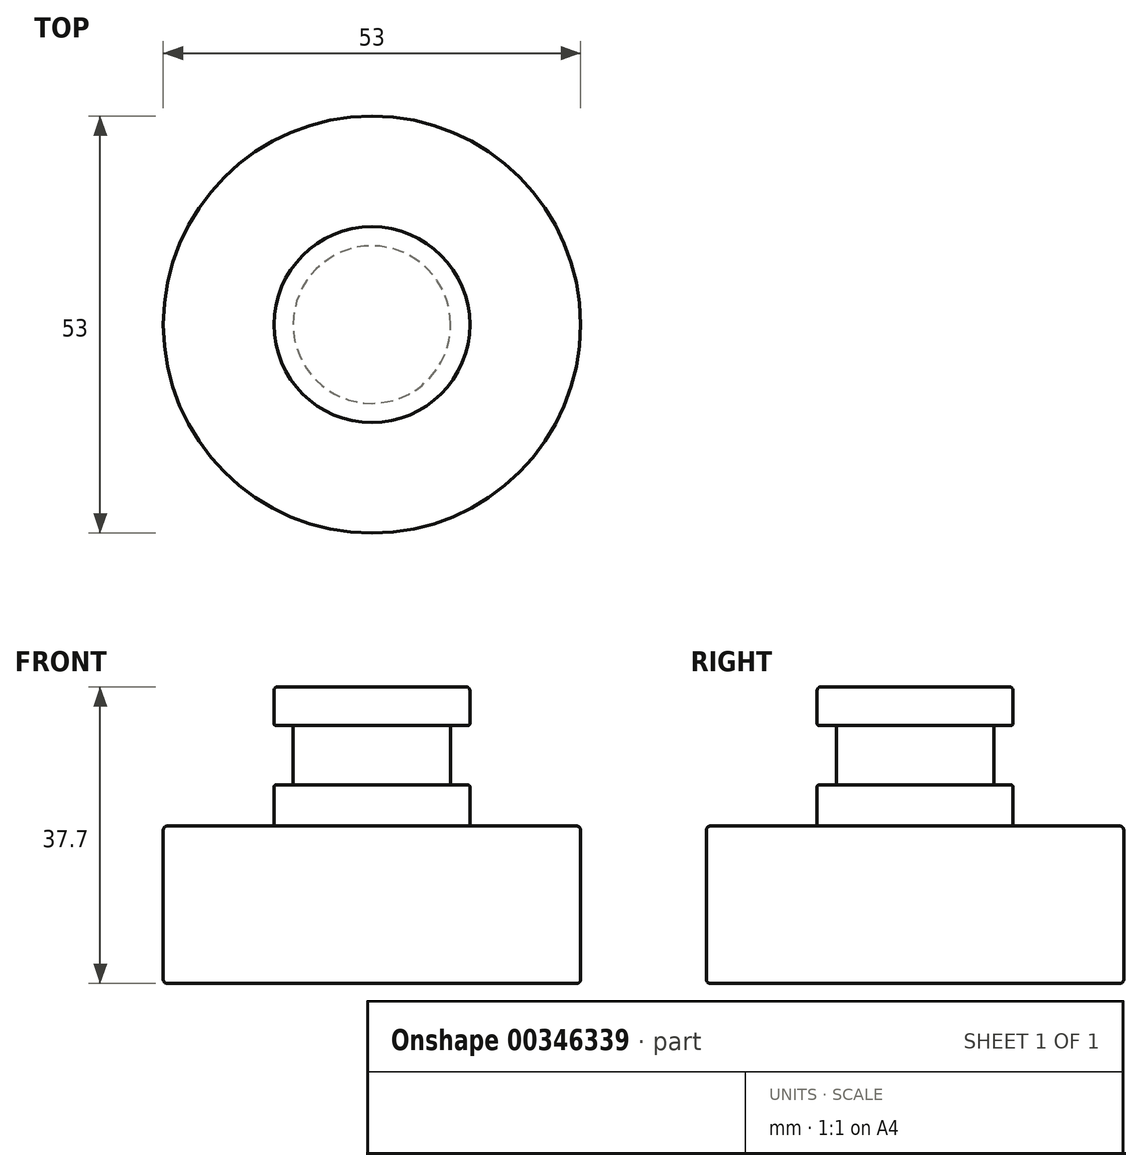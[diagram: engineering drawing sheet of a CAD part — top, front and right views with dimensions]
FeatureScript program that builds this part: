
annotation { "Feature Type Name" : "Feature", "Feature Type Description" : "" }
export const myFeature = defineFeature(function(context is Context, id is Id, definition is map)
    precondition{}
    {
        {
            var Q0;
            Q0=qCreatedBy(makeId("Top.planeOp"),FACE);
            var sketch = newSketch(context, id + "F0", { "sketchPlane" : qUnion([Q0])});
            skCircle(sketch, "E0", {"center": v(0, 0) * mm, "radius": 26.5 * mm});
            skSolve(sketch);
        }
        {
            var Q0;
            Q0 = qSketchRegion(id + "F0", true);
            extrude(context, id + "F1", {"entities" : qUnion([Q0]), "depth" : 20 * mm});
        }
        {
            var Q0;
            Q0=makeQuery(id+"F1.opExtrude","CAP_FACE",FACE,{"disambiguationData":[OSD([sQuery(id+"F0.wireOp",EDGE,"E0")])],"isStart":false});
            var sketch = newSketch(context, id + "F2", { "sketchPlane" : qUnion([Q0])});
            skCircle(sketch, "E1", {"center": v(0, 0) * mm, "radius": 12.44 * mm});
            skSolve(sketch);
        }
        {
            var Q0;
            Q0 = qSketchRegion(id + "F2", true);
            extrude(context, id + "F3", {"entities" : qUnion([Q0]), "operationType" : NewBodyOperationType.ADD, "depth" : 5.2 * mm});
        }
        {
            var Q0;
            Q0=makeQuery(id+"F3.opExtrude","CAP_FACE",FACE,{"disambiguationData":[OSD([sQuery(id+"F2.wireOp",EDGE,"E1")])],"isStart":false});
            var sketch = newSketch(context, id + "F4", { "sketchPlane" : qUnion([Q0])});
            skCircle(sketch, "E2", {"center": v(0, 0) * mm, "radius": 10 * mm});
            skSolve(sketch);
        }
        {
            var Q0;
            Q0 = qSketchRegion(id + "F4", true);
            extrude(context, id + "F5", {"entities" : qUnion([Q0]), "operationType" : NewBodyOperationType.ADD, "depth" : 7.6 * mm});
        }
        {
            var Q0;
            Q0=makeQuery(id+"F5.opExtrude","CAP_FACE",FACE,{"disambiguationData":[OSD([sQuery(id+"F4.wireOp",EDGE,"E2")])],"isStart":false});
            var sketch = newSketch(context, id + "F6", { "sketchPlane" : qUnion([Q0])});
            skCircle(sketch, "E3", {"center": v(0, 0) * mm, "radius": 12.44 * mm});
            skSolve(sketch);
        }
        {
            var Q0;
            Q0 = qSketchRegion(id + "F6", true);
            extrude(context, id + "F7", {"entities" : qUnion([Q0]), "operationType" : NewBodyOperationType.ADD, "depth" : 4.9 * mm});
        }
        {
            var Q0;
            Q0=makeQuery(id+"F7.opExtrude","CAP_EDGE",EDGE,{"disambiguationData":[OSD([sQuery(id+"F6.wireOp",EDGE,"E3")])],"isStart":false});
            var Q1;
            Q1=makeQuery(id+"F1.opExtrude","CAP_EDGE",EDGE,{"disambiguationData":[OSD([sQuery(id+"F0.wireOp",EDGE,"E0")])],"isStart":false});
            var Q2;
            Q2=makeQuery(id+"F1.opExtrude","CAP_EDGE",EDGE,{"disambiguationData":[OSD([sQuery(id+"F0.wireOp",EDGE,"E0")])],"isStart":true});
            fillet(context, id + "F8", {"entities" : qUnion([Q0, Q1, Q2]), "radius" : .5 * mm, "tangentPropagation" : true, "allowEdgeOverflow" : false});
        }
        {
            var Q0;
            Q0=makeQuery(id+"F3.opExtrude","CAP_EDGE",EDGE,{"disambiguationData":[OSD([sQuery(id+"F2.wireOp",EDGE,"E1")])],"isStart":false});
            var Q1;
            Q1=makeQuery(id+"F7.opExtrude","CAP_EDGE",EDGE,{"disambiguationData":[OSD([sQuery(id+"F6.wireOp",EDGE,"E3")])],"isStart":true});
            fillet(context, id + "F9", {"entities" : qUnion([Q0, Q1]), "radius" : .2 * mm, "tangentPropagation" : true, "allowEdgeOverflow" : false});
        }
    });
